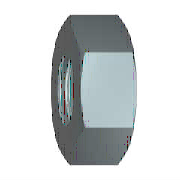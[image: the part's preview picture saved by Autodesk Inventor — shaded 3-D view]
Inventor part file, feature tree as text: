
AUTODESK INVENTOR PART (.ipt)
format: ipt  version: 2019.2 (Build 232265000, 265)  size: 162,304 bytes
history: native  units: mm (DEFAULTED — no unit token found)
features: sketch x3, extrude x1, chamfer x1, hole x1, other x1, plane x1
ambient origin geometry x7: Origin, YZ Plane, XZ Plane, X Axis, Y Axis, Z Axis, Center Point
bodies: Solid1 (feature_tree)
feature tree (8):
  extrude  "Körper"  Depth=1.6mm
  chamfer  "Fase1"  Angle=30.0deg  [1 undecoded]
  hole  "Gewinde"  [1 undecoded]
  other  "Work Axis1"
  plane  "Work Plane1"
  sketch  "Skizze1"  dims[d0=4.618802mm d1=1.6mm]
  sketch  "Skizze2"  dims[d2=0.0mm]
  sketch  "Skizze3"  dims[d3=30.0deg d4=30.0deg d5=3.2mm d6=3.2mm d7=90.0deg d25=1.567mm d26=6.0mm d27=4.0mm d28=2.0mm d29=14.3117mm d30=8.0mm d31=20.594885mm d8=0.216506mm d9=30.0deg d10=0.216506mm d11=30.0deg d13=0.0mm d14=0.0mm d39=0.0mm d40=0.216506mm d41=0.216506mm d42=0.0mm]
note: 2 required parameter values undecoded (feature->parameter linkage not recoverable at this tier; creation-order binding heuristic only, values carry confidence <= 0.55)
